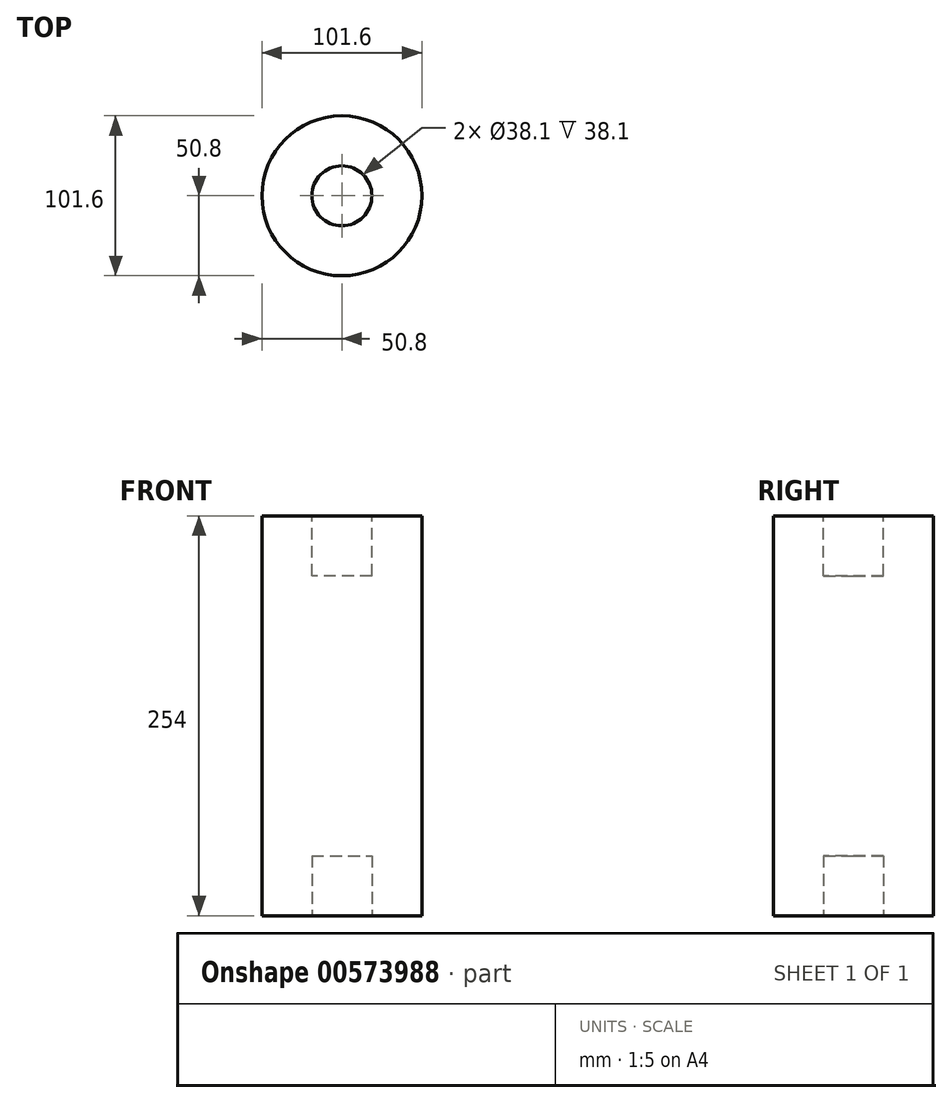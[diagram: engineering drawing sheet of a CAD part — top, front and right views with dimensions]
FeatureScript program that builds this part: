
annotation { "Feature Type Name" : "Feature", "Feature Type Description" : "" }
export const myFeature = defineFeature(function(context is Context, id is Id, definition is map)
    precondition{}
    {
        {
            var Q0;
            Q0=qCreatedBy(makeId("Front.planeOp"),FACE);
            var sketch = newSketch(context, id + "F0", { "sketchPlane" : qUnion([Q0])});
            skLineSegment(sketch, "E0.bottom", {"start": v(-25.4, 127) * mm, "end": v(25.4, 127) * mm});
            skLineSegment(sketch, "E0.top", {"start": v(-25.4, -127) * mm, "end": v(25.4, -127) * mm});
            skLineSegment(sketch, "E0.left", {"start": v(-25.4, 127) * mm, "end": v(-25.4, -127) * mm});
            skLineSegment(sketch, "E0.right", {"start": v(25.4, 127) * mm, "end": v(25.4, -127) * mm});
            skPoint(sketch, "E0.middle", {"position": v(0, 0) * mm});
            skLineSegment(sketch, "E1.bottom", {"start": v(-25.4, 127) * mm, "end": v(-12.7, 127) * mm});
            skLineSegment(sketch, "E1.top", {"start": v(-25.4, -127) * mm, "end": v(-12.7, -127) * mm});
            skLineSegment(sketch, "E1.right", {"start": v(-12.7, 127) * mm, "end": v(-12.7, -127) * mm});
            skSolve(sketch);
        }
        {
            var Q0;
            Q0=makeQuery(id+"F0.imprint","IMPRINT",FACE,{"disambiguationData":[TD([[makeQuery(id+"F0.imprint","IMPRINT",EDGE,{"derivedFrom":sQuery(id+"F0.wireOp",EDGE,"E0.bottom")}),-1.0]])]});
            var Q1;
            Q1=sQuery(id+"F0.wireOp",EDGE,"E0.left");
            revolve(context, id + "F1", {"entities" : qUnion([Q0]), "axis" : qUnion([Q1]), "revolveType" : RevolveType.FULL});
        }
        {
            var Q0;
            Q0=makeQuery(id+"F1.opRevolve","SWEPT_FACE",FACE,{"disambiguationData":[OSD([sQuery(id+"F0.wireOp",EDGE,"E0.bottom")])]});
            var sketch = newSketch(context, id + "F2", { "sketchPlane" : qUnion([Q0])});
            skCircle(sketch, "E2", {"center": v(-25.4, 0) * mm, "radius": 19.05 * mm});
            skSolve(sketch);
        }
        {
            var Q0;
            Q0=makeQuery(id+"F2.imprint","IMPRINT",FACE,{"disambiguationData":[TD([[makeQuery(id+"F2.imprint","IMPRINT",EDGE,{"derivedFrom":sQuery(id+"F2.wireOp",EDGE,"E2")}),1.0]])]});
            extrude(context, id + "F3", {"entities" : qUnion([Q0]), "operationType" : NewBodyOperationType.REMOVE, "oppositeDirection" : true, "depth" : 38.1 * mm, "offsetDistance" : 25.4 * mm});
        }
        {
            var Q0;
            Q0=makeQuery(id+"F1.opRevolve","SWEPT_FACE",FACE,{"disambiguationData":[OSD([sQuery(id+"F0.wireOp",EDGE,"E0.top")])]});
            var sketch = newSketch(context, id + "F4", { "sketchPlane" : qUnion([Q0])});
            skCircle(sketch, "E3", {"center": v(-25.4, 0) * mm, "radius": 19.05 * mm});
            skSolve(sketch);
        }
        {
            var Q0;
            Q0=makeQuery(id+"F4.imprint","IMPRINT",FACE,{"disambiguationData":[TD([[makeQuery(id+"F4.imprint","IMPRINT",EDGE,{"derivedFrom":sQuery(id+"F4.wireOp",EDGE,"E3")}),1.0]])]});
            extrude(context, id + "F5", {"entities" : qUnion([Q0]), "operationType" : NewBodyOperationType.REMOVE, "oppositeDirection" : true, "depth" : 38.1 * mm, "offsetDistance" : 25.4 * mm});
        }
    });
